AUTODESK INVENTOR PART (.ipt)
format: ipt  version: 2024 (Build 280153000, 153)  size: 282,624 bytes
history: native  units: in
note: dims shown in document units (in); Inventor stores cm internally (conversion verified against a paired STEP export)
features: sketch x1
ambient origin geometry x8: Origin, YZ Plane, XZ Plane, XY Plane, X Axis, Y Axis, Z Axis, Center Point
feature tree (1):
  sketch  "Sketch1"  dims[d0=45.0deg d1=0.0787in d3=1.9685in d5=0.0787in d6=0.3937in d8=0.3937in d10=0.2756in d11=2.3622in d13=0.0787in d14=0.3937in d16=0.3937in d18=0.3346in d19=0.0127in d20=0.0024in d21=0.0787in d23=0.2756in d24=0.315in d25=0.0225in d26=0.2953in]
